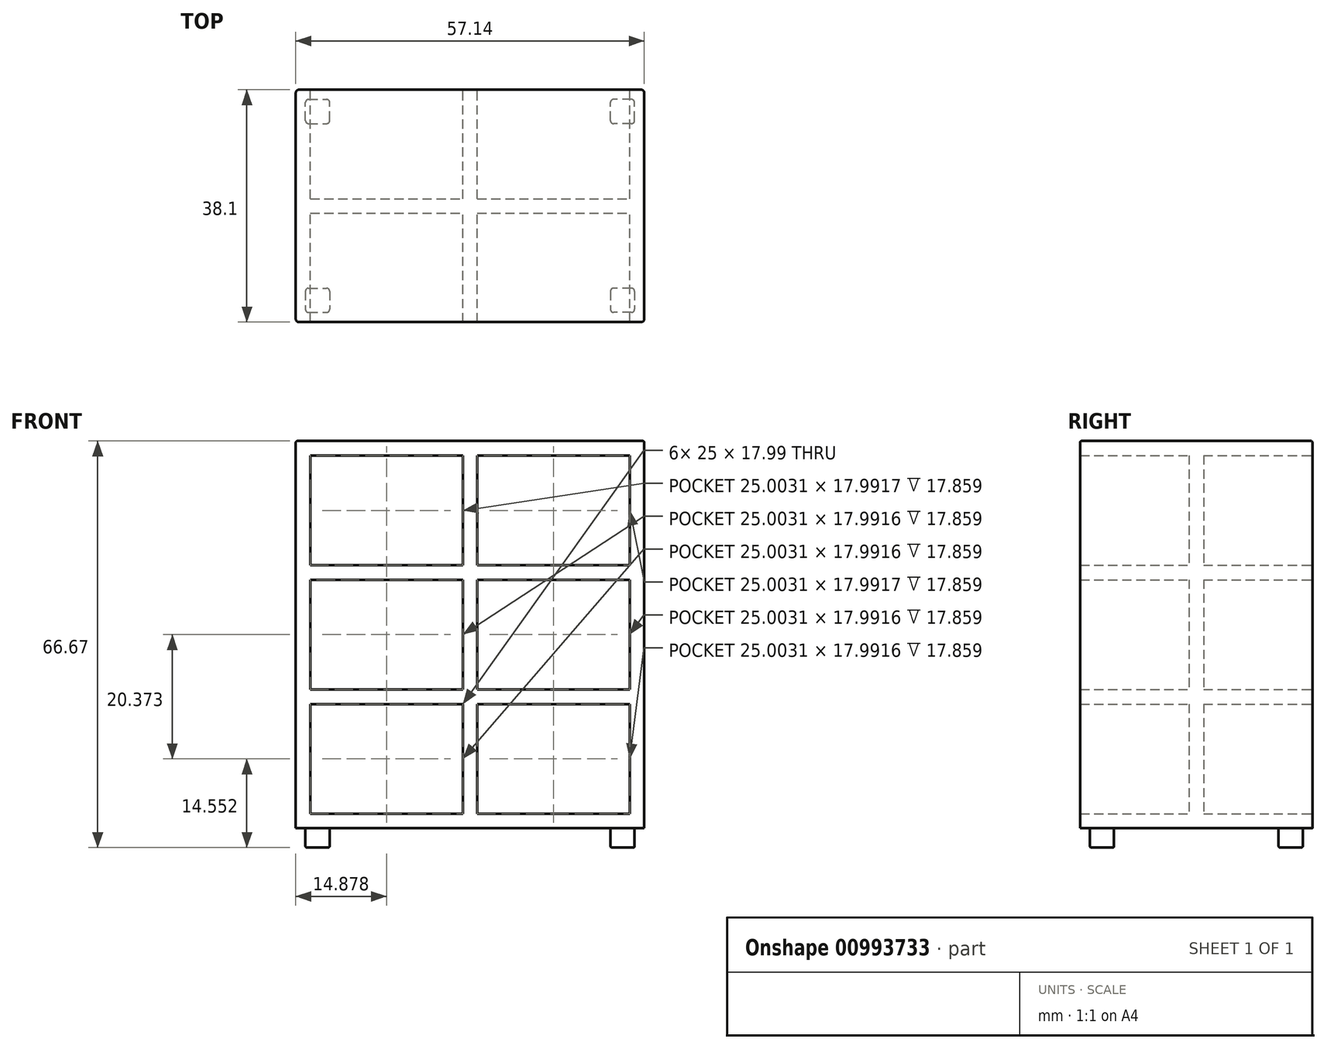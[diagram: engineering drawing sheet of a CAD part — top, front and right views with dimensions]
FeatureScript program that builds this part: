
annotation { "Feature Type Name" : "Feature", "Feature Type Description" : "" }
export const myFeature = defineFeature(function(context is Context, id is Id, definition is map)
    precondition{}
    {
        {
            var Q0;
            Q0=qCreatedBy(makeId("Front.planeOp"),FACE);
            var sketch = newSketch(context, id + "F0", { "sketchPlane" : qUnion([Q0])});
            skLineSegment(sketch, "E0", {"start": v(0, 0) * mm, "end": v(0, 1066.8) * mm, "construction": true});
            skLineSegment(sketch, "E1.bottom", {"start": v(-457.2, 0) * mm, "end": v(457.2, 0) * mm});
            skLineSegment(sketch, "E1.top", {"start": v(-457.2, 1066.8) * mm, "end": v(457.2, 1066.8) * mm});
            skLineSegment(sketch, "E1.left", {"start": v(-457.2, 0) * mm, "end": v(-457.2, 1066.8) * mm});
            skLineSegment(sketch, "E1.right", {"start": v(457.2, 0) * mm, "end": v(457.2, 1066.8) * mm});
            skLineSegment(sketch, "E2", {"start": v(-457.2, 50.8) * mm, "end": v(457.2, 50.8) * mm});
            skLineSegment(sketch, "E3.bottom", {"start": v(-406.4, 50.8) * mm, "end": v(-355.6, 50.8) * mm});
            skLineSegment(sketch, "E3.top", {"start": v(-406.4, 0) * mm, "end": v(-355.6, 0) * mm});
            skLineSegment(sketch, "E3.left", {"start": v(-406.4, 50.8) * mm, "end": v(-406.4, 0) * mm});
            skLineSegment(sketch, "E3.right", {"start": v(-355.6, 50.8) * mm, "end": v(-355.6, 0) * mm});
            skLineSegment(sketch, "E4.bottom", {"start": v(-419.1, 1028.7) * mm, "end": v(-19.05, 1028.7) * mm});
            skLineSegment(sketch, "E4.top", {"start": v(-419.1, 740.83) * mm, "end": v(-19.05, 740.83) * mm});
            skLineSegment(sketch, "E4.left", {"start": v(-419.1, 1028.7) * mm, "end": v(-419.1, 740.83) * mm});
            skLineSegment(sketch, "E4.right", {"start": v(-19.05, 1028.7) * mm, "end": v(-19.05, 740.83) * mm});
            skLineSegment(sketch, "E5.bottom", {"start": v(-419.1, 702.73) * mm, "end": v(-19.05, 702.73) * mm});
            skLineSegment(sketch, "E5.top", {"start": v(-419.1, 414.87) * mm, "end": v(-19.05, 414.87) * mm});
            skLineSegment(sketch, "E5.left", {"start": v(-419.1, 702.73) * mm, "end": v(-419.1, 414.87) * mm});
            skLineSegment(sketch, "E5.right", {"start": v(-19.05, 702.73) * mm, "end": v(-19.05, 414.87) * mm});
            skLineSegment(sketch, "E6.bottom", {"start": v(-419.1, 376.77) * mm, "end": v(-19.05, 376.77) * mm});
            skLineSegment(sketch, "E6.top", {"start": v(-419.1, 88.9) * mm, "end": v(-19.05, 88.9) * mm});
            skLineSegment(sketch, "E6.left", {"start": v(-419.1, 376.77) * mm, "end": v(-419.1, 88.9) * mm});
            skLineSegment(sketch, "E6.right", {"start": v(-19.05, 376.77) * mm, "end": v(-19.05, 88.9) * mm});
            skLineSegment(sketch, "E7", {"start": v(-419.1, 1028.7) * mm, "end": v(-419.1, 1066.8) * mm, "construction": true});
            skLineSegment(sketch, "E8", {"start": v(-419.1, 740.83) * mm, "end": v(-419.1, 702.73) * mm, "construction": true});
            skLineSegment(sketch, "E9", {"start": v(-419.1, 414.87) * mm, "end": v(-419.1, 376.77) * mm, "construction": true});
            skLineSegment(sketch, "E10", {"start": v(-419.1, 88.9) * mm, "end": v(-419.1, 50.8) * mm, "construction": true});
            skLineSegment(sketch, "E11", {"start": v(-419.1, 1028.7) * mm, "end": v(-457.2, 1028.7) * mm, "construction": true});
            skLineSegment(sketch, "E12", {"start": v(-19.05, 1028.7) * mm, "end": v(19.05, 1028.7) * mm, "construction": true});
            skLineSegment(sketch, "E13.bottom", {"start": v(19.05, 1028.7) * mm, "end": v(419.1, 1028.7) * mm});
            skLineSegment(sketch, "E13.top", {"start": v(19.05, 740.83) * mm, "end": v(419.1, 740.83) * mm});
            skLineSegment(sketch, "E13.left", {"start": v(19.05, 1028.7) * mm, "end": v(19.05, 740.83) * mm});
            skLineSegment(sketch, "E13.right", {"start": v(419.1, 1028.7) * mm, "end": v(419.1, 740.83) * mm});
            skLineSegment(sketch, "E14.bottom", {"start": v(19.05, 702.73) * mm, "end": v(419.1, 702.73) * mm});
            skLineSegment(sketch, "E14.top", {"start": v(19.05, 414.87) * mm, "end": v(419.1, 414.87) * mm});
            skLineSegment(sketch, "E14.left", {"start": v(19.05, 702.73) * mm, "end": v(19.05, 414.87) * mm});
            skLineSegment(sketch, "E14.right", {"start": v(419.1, 702.73) * mm, "end": v(419.1, 414.87) * mm});
            skLineSegment(sketch, "E15.bottom", {"start": v(19.05, 376.77) * mm, "end": v(419.1, 376.77) * mm});
            skLineSegment(sketch, "E15.top", {"start": v(19.05, 88.9) * mm, "end": v(419.1, 88.9) * mm});
            skLineSegment(sketch, "E15.left", {"start": v(19.05, 376.77) * mm, "end": v(19.05, 88.9) * mm});
            skLineSegment(sketch, "E15.right", {"start": v(419.1, 376.77) * mm, "end": v(419.1, 88.9) * mm});
            skLineSegment(sketch, "E16.MirrorCS", {"start": v(406.4, 50.8) * mm, "end": v(406.4, 0) * mm});
            skLineSegment(sketch, "E17.MirrorCS", {"start": v(355.6, 50.8) * mm, "end": v(355.6, 0) * mm});
            skSolve(sketch);
        }
        {
            var Q0;
            {var subQ1=sQuery(id+"F0.wireOp",EDGE,"E1.top");Q0=makeQuery(id+"F0.imprint","IMPRINT",FACE,{"disambiguationData":[TD([[makeQuery(id+"F0.imprint","IMPRINT",EDGE,{"derivedFrom":subQ1}),-1.0]])]});}
            extrude(context, id + "F1", {"entities" : qUnion([Q0]), "endBound" : BoundingType.SYMMETRIC, "depth" : 609.6 * mm, "offsetDistance" : 25.4 * mm});
        }
        {
            var Q0;
            Q0=makeQuery(id+"F0.imprint","IMPRINT",FACE,{"disambiguationData":[TD([[makeQuery(id+"F0.imprint","IMPRINT",EDGE,{"derivedFrom":sQuery(id+"F0.wireOp",EDGE,"E4.bottom")}),-1.0]])]});
            var Q1;
            Q1=makeQuery(id+"F0.imprint","IMPRINT",FACE,{"disambiguationData":[TD([[makeQuery(id+"F0.imprint","IMPRINT",EDGE,{"derivedFrom":sQuery(id+"F0.wireOp",EDGE,"E13.bottom")}),-1.0]])]});
            var Q2;
            Q2=makeQuery(id+"F0.imprint","IMPRINT",FACE,{"disambiguationData":[TD([[makeQuery(id+"F0.imprint","IMPRINT",EDGE,{"derivedFrom":sQuery(id+"F0.wireOp",EDGE,"E14.bottom")}),-1.0]])]});
            var Q3;
            Q3=makeQuery(id+"F0.imprint","IMPRINT",FACE,{"disambiguationData":[TD([[makeQuery(id+"F0.imprint","IMPRINT",EDGE,{"derivedFrom":sQuery(id+"F0.wireOp",EDGE,"E5.bottom")}),-1.0]])]});
            var Q4;
            Q4=makeQuery(id+"F0.imprint","IMPRINT",FACE,{"disambiguationData":[TD([[makeQuery(id+"F0.imprint","IMPRINT",EDGE,{"derivedFrom":sQuery(id+"F0.wireOp",EDGE,"E15.bottom")}),-1.0]])]});
            var Q5;
            Q5=makeQuery(id+"F0.imprint","IMPRINT",FACE,{"disambiguationData":[TD([[makeQuery(id+"F0.imprint","IMPRINT",EDGE,{"derivedFrom":sQuery(id+"F0.wireOp",EDGE,"E6.bottom")}),-1.0]])]});
            extrude(context, id + "F2", {"entities" : qUnion([Q0, Q1, Q2, Q3, Q4, Q5]), "operationType" : NewBodyOperationType.ADD, "endBound" : BoundingType.SYMMETRIC, "depth" : 38.1 * mm, "offsetDistance" : 25.4 * mm});
        }
        {
            var Q0;
            Q0=qCreatedBy(makeId("Top.planeOp"),FACE);
            var sketch = newSketch(context, id + "F3", { "sketchPlane" : qUnion([Q0])});
            skLineSegment(sketch, "E18.bottom", {"start": v(-431.8, -215.9) * mm, "end": v(-368.3, -215.9) * mm});
            skLineSegment(sketch, "E18.top", {"start": v(-431.8, -279.4) * mm, "end": v(-368.3, -279.4) * mm});
            skLineSegment(sketch, "E18.left", {"start": v(-431.8, -215.9) * mm, "end": v(-431.8, -279.4) * mm});
            skLineSegment(sketch, "E18.right", {"start": v(-368.3, -215.9) * mm, "end": v(-368.3, -279.4) * mm});
            skLineSegment(sketch, "E19", {"start": v(-431.8, -215.9) * mm, "end": v(-457.2, -215.9) * mm, "construction": true});
            skLineSegment(sketch, "E20", {"start": v(0, -304.8) * mm, "end": v(0, 0) * mm, "construction": true});
            skLineSegment(sketch, "E21", {"start": v(0, 0) * mm, "end": v(-457.2, 0) * mm, "construction": true});
            skLineSegment(sketch, "E22.MirrorCS", {"start": v(431.8, -279.4) * mm, "end": v(368.3, -279.4) * mm});
            skLineSegment(sketch, "E23.MirrorCS", {"start": v(368.3, -215.9) * mm, "end": v(368.3, -279.4) * mm});
            skLineSegment(sketch, "E24.MirrorCS", {"start": v(431.8, -215.9) * mm, "end": v(368.3, -215.9) * mm});
            skLineSegment(sketch, "E25.MirrorCS", {"start": v(431.8, -215.9) * mm, "end": v(431.8, -279.4) * mm});
            skLineSegment(sketch, "E26.MirrorCS", {"start": v(431.8, 279.4) * mm, "end": v(368.3, 279.4) * mm});
            skLineSegment(sketch, "E27.MirrorCS", {"start": v(-431.8, 215.9) * mm, "end": v(-431.8, 279.4) * mm});
            skLineSegment(sketch, "E28.MirrorCS", {"start": v(431.8, 215.9) * mm, "end": v(431.8, 279.4) * mm});
            skLineSegment(sketch, "E29.MirrorCS", {"start": v(-431.8, 215.9) * mm, "end": v(-368.3, 215.9) * mm});
            skLineSegment(sketch, "E30.MirrorCS", {"start": v(368.3, 215.9) * mm, "end": v(368.3, 279.4) * mm});
            skLineSegment(sketch, "E31.MirrorCS", {"start": v(431.8, 215.9) * mm, "end": v(368.3, 215.9) * mm});
            skLineSegment(sketch, "E32.MirrorCS", {"start": v(-431.8, 279.4) * mm, "end": v(-368.3, 279.4) * mm});
            skLineSegment(sketch, "E33.MirrorCS", {"start": v(-368.3, 215.9) * mm, "end": v(-368.3, 279.4) * mm});
            skLineSegment(sketch, "E34", {"start": v(-431.8, -279.4) * mm, "end": v(-431.8, -304.8) * mm, "construction": true});
            skSolve(sketch);
        }
        {
            var Q0;
            Q0=makeQuery(id+"F3.imprint","IMPRINT",FACE,{"disambiguationData":[TD([[makeQuery(id+"F3.imprint","IMPRINT",EDGE,{"derivedFrom":sQuery(id+"F3.wireOp",EDGE,"E18.bottom")}),-1.0]])]});
            var Q1;
            Q1=makeQuery(id+"F3.imprint","IMPRINT",FACE,{"disambiguationData":[TD([[makeQuery(id+"F3.imprint","IMPRINT",EDGE,{"derivedFrom":sQuery(id+"F3.wireOp",EDGE,"E22.MirrorCS")}),-1.0]])]});
            var Q2;
            Q2=makeQuery(id+"F3.imprint","IMPRINT",FACE,{"disambiguationData":[TD([[makeQuery(id+"F3.imprint","IMPRINT",EDGE,{"derivedFrom":sQuery(id+"F3.wireOp",EDGE,"E26.MirrorCS")}),1.0]])]});
            var Q3;
            Q3=makeQuery(id+"F3.imprint","IMPRINT",FACE,{"disambiguationData":[TD([[makeQuery(id+"F3.imprint","IMPRINT",EDGE,{"derivedFrom":sQuery(id+"F3.wireOp",EDGE,"E27.MirrorCS")}),-1.0]])]});
            extrude(context, id + "F4", {"entities" : qUnion([Q0, Q1, Q2, Q3]), "operationType" : NewBodyOperationType.ADD, "endBound" : BoundingType.UP_TO_NEXT, "depth" : 50.8 * mm, "offsetDistance" : 25.4 * mm});
        }
        {
            var Q0;
            Q0=makeQuery(id+"F1.opExtrude","SWEPT_BODY",BODY,{"disambiguationData":[OSD([sQuery(id+"F0.wireOp",EDGE,"E1.top"),sQuery(id+"F0.wireOp",EDGE,"E1.left"),sQuery(id+"F0.wireOp",EDGE,"E1.right"),sQuery(id+"F0.wireOp",EDGE,"E2"),sQuery(id+"F0.wireOp",EDGE,"E3.bottom"),sQuery(id+"F0.wireOp",EDGE,"E4.bottom"),sQuery(id+"F0.wireOp",EDGE,"E4.top"),sQuery(id+"F0.wireOp",EDGE,"E4.left"),sQuery(id+"F0.wireOp",EDGE,"E4.right"),sQuery(id+"F0.wireOp",EDGE,"E5.bottom"),sQuery(id+"F0.wireOp",EDGE,"E5.top"),sQuery(id+"F0.wireOp",EDGE,"E5.left"),sQuery(id+"F0.wireOp",EDGE,"E5.right"),sQuery(id+"F0.wireOp",EDGE,"E6.bottom"),sQuery(id+"F0.wireOp",EDGE,"E6.top"),sQuery(id+"F0.wireOp",EDGE,"E6.left"),sQuery(id+"F0.wireOp",EDGE,"E6.right"),sQuery(id+"F0.wireOp",EDGE,"E13.bottom"),sQuery(id+"F0.wireOp",EDGE,"E13.top"),sQuery(id+"F0.wireOp",EDGE,"E13.left"),sQuery(id+"F0.wireOp",EDGE,"E13.right"),sQuery(id+"F0.wireOp",EDGE,"E14.bottom"),sQuery(id+"F0.wireOp",EDGE,"E14.top"),sQuery(id+"F0.wireOp",EDGE,"E14.left"),sQuery(id+"F0.wireOp",EDGE,"E14.right"),sQuery(id+"F0.wireOp",EDGE,"E15.bottom"),sQuery(id+"F0.wireOp",EDGE,"E15.top"),sQuery(id+"F0.wireOp",EDGE,"E15.left"),sQuery(id+"F0.wireOp",EDGE,"E15.right")])]});
            var Q1;
            Q1=sQuery(id+"F0.wireOp",VERTEX,"E0.start");
            transform(context, id + "F5", {"entities" : qUnion([Q0]), "transformType" : TransformType.SCALE_UNIFORMLY, "scale" : 1 / 16, "scalePoint" : qUnion([Q1]), "makeCopy" : false});
        }
        {
            var Q0;
            Q0=makeQuery(id+"F1.opExtrude","CAP_EDGE",EDGE,{"disambiguationData":[OSD([sQuery(id+"F0.wireOp",EDGE,"E1.right")])],"isStart":false});
            var Q1;
            Q1=makeQuery(id+"F1.opExtrude","CAP_EDGE",EDGE,{"disambiguationData":[OSD([sQuery(id+"F0.wireOp",EDGE,"E1.right")])],"isStart":true});
            var Q2;
            Q2=makeQuery(id+"F1.opExtrude","CAP_EDGE",EDGE,{"disambiguationData":[OSD([sQuery(id+"F0.wireOp",EDGE,"E1.left")])],"isStart":false});
            var Q3;
            Q3=makeQuery(id+"F1.opExtrude","CAP_EDGE",EDGE,{"disambiguationData":[OSD([sQuery(id+"F0.wireOp",EDGE,"E1.left")])],"isStart":true});
            var Q4;
            Q4=makeQuery(id+"F4.opExtrude","SWEPT_EDGE",EDGE,{"disambiguationData":[OSD([sQuery(id+"F3.wireOp",EDGE,"E26.MirrorCS"),sQuery(id+"F3.wireOp",EDGE,"E28.MirrorCS")])]});
            var Q5;
            Q5=makeQuery(id+"F4.opExtrude","SWEPT_EDGE",EDGE,{"disambiguationData":[OSD([sQuery(id+"F3.wireOp",EDGE,"E28.MirrorCS"),sQuery(id+"F3.wireOp",EDGE,"E31.MirrorCS")])]});
            var Q6;
            Q6=makeQuery(id+"F4.opExtrude","SWEPT_EDGE",EDGE,{"disambiguationData":[OSD([sQuery(id+"F3.wireOp",EDGE,"E26.MirrorCS"),sQuery(id+"F3.wireOp",EDGE,"E30.MirrorCS")])]});
            var Q7;
            Q7=makeQuery(id+"F4.opExtrude","SWEPT_EDGE",EDGE,{"disambiguationData":[OSD([sQuery(id+"F3.wireOp",EDGE,"E30.MirrorCS"),sQuery(id+"F3.wireOp",EDGE,"E31.MirrorCS")])]});
            var Q8;
            Q8=makeQuery(id+"F4.opExtrude","SWEPT_EDGE",EDGE,{"disambiguationData":[OSD([sQuery(id+"F3.wireOp",EDGE,"E23.MirrorCS"),sQuery(id+"F3.wireOp",EDGE,"E24.MirrorCS")])]});
            var Q9;
            Q9=makeQuery(id+"F4.opExtrude","SWEPT_EDGE",EDGE,{"disambiguationData":[OSD([sQuery(id+"F3.wireOp",EDGE,"E24.MirrorCS"),sQuery(id+"F3.wireOp",EDGE,"E25.MirrorCS")])]});
            var Q10;
            Q10=makeQuery(id+"F4.opExtrude","SWEPT_EDGE",EDGE,{"disambiguationData":[OSD([sQuery(id+"F3.wireOp",EDGE,"E22.MirrorCS"),sQuery(id+"F3.wireOp",EDGE,"E25.MirrorCS")])]});
            var Q11;
            Q11=makeQuery(id+"F4.opExtrude","SWEPT_EDGE",EDGE,{"disambiguationData":[OSD([sQuery(id+"F3.wireOp",EDGE,"E22.MirrorCS"),sQuery(id+"F3.wireOp",EDGE,"E23.MirrorCS")])]});
            var Q12;
            Q12=makeQuery(id+"F4.opExtrude","SWEPT_EDGE",EDGE,{"disambiguationData":[OSD([sQuery(id+"F3.wireOp",EDGE,"E18.top"),sQuery(id+"F3.wireOp",EDGE,"E18.right")])]});
            var Q13;
            Q13=makeQuery(id+"F4.opExtrude","SWEPT_EDGE",EDGE,{"disambiguationData":[OSD([sQuery(id+"F3.wireOp",EDGE,"E18.bottom"),sQuery(id+"F3.wireOp",EDGE,"E18.right")])]});
            var Q14;
            Q14=makeQuery(id+"F4.opExtrude","SWEPT_EDGE",EDGE,{"disambiguationData":[OSD([sQuery(id+"F3.wireOp",EDGE,"E18.top"),sQuery(id+"F3.wireOp",EDGE,"E18.left")])]});
            var Q15;
            Q15=makeQuery(id+"F4.opExtrude","SWEPT_EDGE",EDGE,{"disambiguationData":[OSD([sQuery(id+"F3.wireOp",EDGE,"E18.bottom"),sQuery(id+"F3.wireOp",EDGE,"E18.left")])]});
            var Q16;
            Q16=makeQuery(id+"F4.opExtrude","SWEPT_EDGE",EDGE,{"disambiguationData":[OSD([sQuery(id+"F3.wireOp",EDGE,"E32.MirrorCS"),sQuery(id+"F3.wireOp",EDGE,"E33.MirrorCS")])]});
            var Q17;
            Q17=makeQuery(id+"F4.opExtrude","SWEPT_EDGE",EDGE,{"disambiguationData":[OSD([sQuery(id+"F3.wireOp",EDGE,"E29.MirrorCS"),sQuery(id+"F3.wireOp",EDGE,"E33.MirrorCS")])]});
            var Q18;
            Q18=makeQuery(id+"F4.opExtrude","SWEPT_EDGE",EDGE,{"disambiguationData":[OSD([sQuery(id+"F3.wireOp",EDGE,"E27.MirrorCS"),sQuery(id+"F3.wireOp",EDGE,"E29.MirrorCS")])]});
            var Q19;
            Q19=makeQuery(id+"F4.opExtrude","SWEPT_EDGE",EDGE,{"disambiguationData":[OSD([sQuery(id+"F3.wireOp",EDGE,"E27.MirrorCS"),sQuery(id+"F3.wireOp",EDGE,"E32.MirrorCS")])]});
            fillet(context, id + "F6", {"entities" : qUnion([Q0, Q1, Q2, Q3, Q4, Q5, Q6, Q7, Q8, Q9, Q10, Q11, Q12, Q13, Q14, Q15, Q16, Q17, Q18, Q19]), "radius" : 0.5 * mm, "tangentPropagation" : true, "allowEdgeOverflow" : false});
        }
        {
            var Q0;
            Q0=makeQuery(id+"F1.opExtrude","SWEPT_EDGE",EDGE,{"disambiguationData":[OSD([sQuery(id+"F0.wireOp",EDGE,"E1.top"),sQuery(id+"F0.wireOp",EDGE,"E1.left")])]});
            var Q1;
            Q1=makeQuery(id+"F4.opExtrude","CAP_EDGE",EDGE,{"disambiguationData":[OSD([sQuery(id+"F3.wireOp",EDGE,"E27.MirrorCS")])],"isStart":true});
            var Q2;
            Q2=makeQuery(id+"F4.opExtrude","CAP_EDGE",EDGE,{"disambiguationData":[OSD([sQuery(id+"F3.wireOp",EDGE,"E18.bottom")])],"isStart":true});
            var Q3;
            Q3=makeQuery(id+"F4.opExtrude","CAP_EDGE",EDGE,{"disambiguationData":[OSD([sQuery(id+"F3.wireOp",EDGE,"E22.MirrorCS")])],"isStart":true});
            var Q4;
            Q4=makeQuery(id+"F4.opExtrude","CAP_EDGE",EDGE,{"disambiguationData":[OSD([sQuery(id+"F3.wireOp",EDGE,"E31.MirrorCS")])],"isStart":true});
            var Q5;
            Q5=makeQuery(id+"F4.opExtrude","CAP_EDGE",EDGE,{"disambiguationData":[OSD([sQuery(id+"F3.wireOp",EDGE,"E33.MirrorCS")])],"isStart":false});
            var Q6;
            Q6=makeQuery(id+"F4.opExtrude","CAP_EDGE",EDGE,{"disambiguationData":[OSD([sQuery(id+"F3.wireOp",EDGE,"E18.right")])],"isStart":false});
            var Q7;
            Q7=makeQuery(id+"F4.opExtrude","CAP_EDGE",EDGE,{"disambiguationData":[OSD([sQuery(id+"F3.wireOp",EDGE,"E24.MirrorCS")])],"isStart":false});
            var Q8;
            Q8=makeQuery(id+"F4.opExtrude","CAP_EDGE",EDGE,{"disambiguationData":[OSD([sQuery(id+"F3.wireOp",EDGE,"E28.MirrorCS")])],"isStart":false});
            fillet(context, id + "F7", {"entities" : qUnion([Q0, Q1, Q2, Q3, Q4, Q5, Q6, Q7, Q8]), "radius" : 0.25 * mm, "tangentPropagation" : true, "allowEdgeOverflow" : false});
        }
    });
